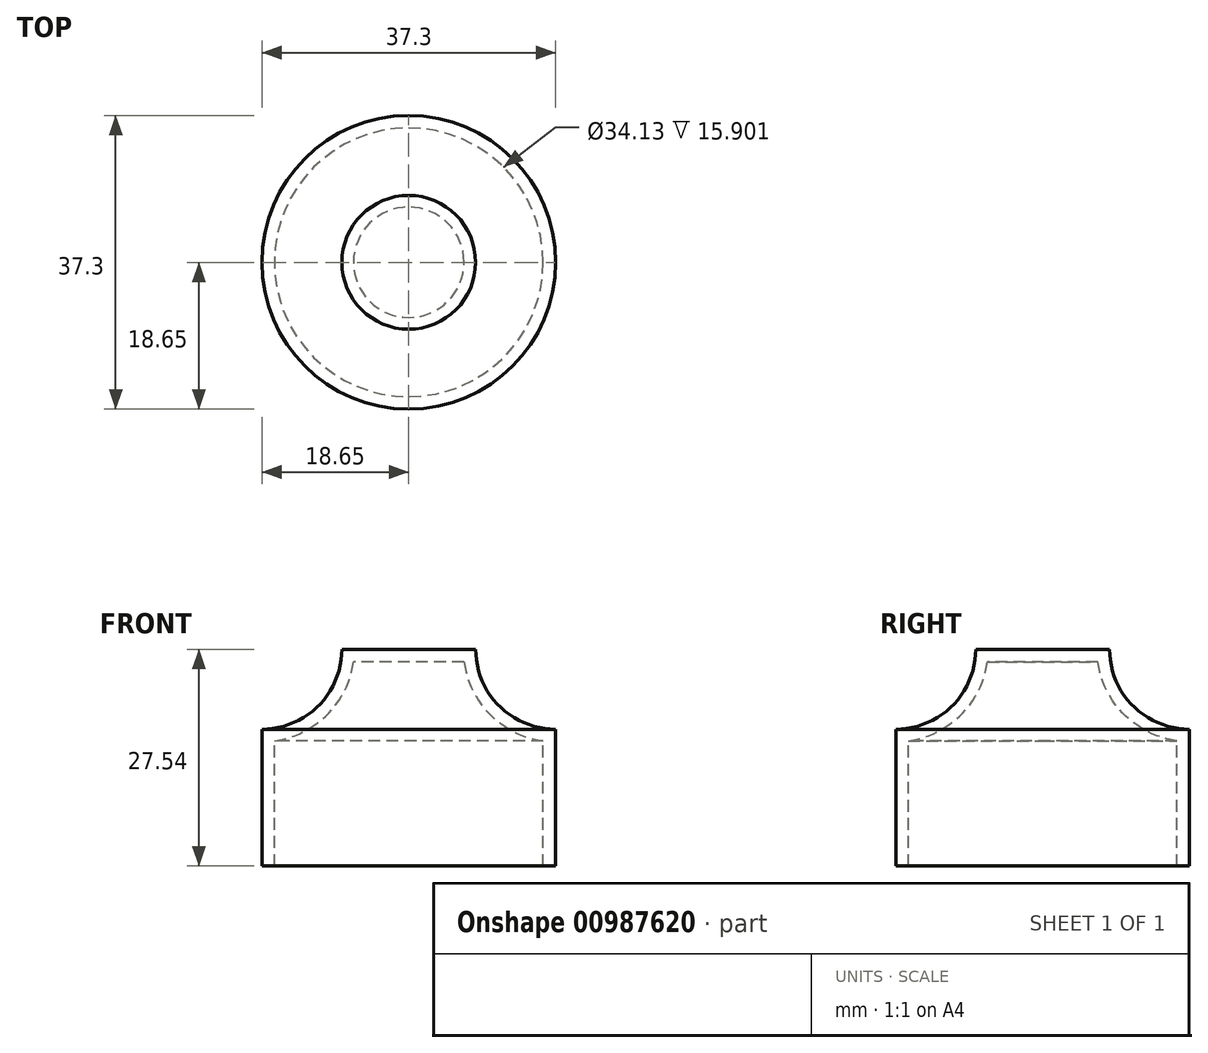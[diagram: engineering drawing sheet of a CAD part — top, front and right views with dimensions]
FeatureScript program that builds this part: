
annotation { "Feature Type Name" : "Feature", "Feature Type Description" : "" }
export const myFeature = defineFeature(function(context is Context, id is Id, definition is map)
    precondition{}
    {
        {
            var Q0;
            Q0=qCreatedBy(makeId("Front.planeOp"),FACE);
            var sketch = newSketch(context, id + "F0", { "sketchPlane" : qUnion([Q0])});
            skLineSegment(sketch, "E0", {"start": v(18.65, 0) * mm, "end": v(18.65, 17.38) * mm});
            skArc(sketch, "E1", {"start": v(8.5, 27.54) * mm, "mid": v(11.47, 20.36) * mm, "end": v(18.65, 17.38) * mm});
            skLineSegment(sketch, "E2", {"start": v(18.65, 17.38) * mm, "end": v(30.29, 17.38) * mm, "construction": true});
            skLineSegment(sketch, "E3", {"start": v(8.5, 27.54) * mm, "end": v(0, 27.54) * mm});
            skLineSegment(sketch, "E4", {"start": v(0, 27.54) * mm, "end": v(0, 25.95) * mm});
            skLineSegment(sketch, "E5", {"start": v(8.5, 27.54) * mm, "end": v(8.5, 39.33) * mm, "construction": true});
            skLineSegment(sketch, "E6.0", {"start": v(7.02, 25.95) * mm, "end": v(0, 25.95) * mm});
            skArc(sketch, "E6.1", {"start": v(7.02, 25.95) * mm, "mid": v(10.35, 19.23) * mm, "end": v(17.07, 15.9) * mm});
            skLineSegment(sketch, "E6.2", {"start": v(17.07, 0) * mm, "end": v(17.07, 15.9) * mm});
            skLineSegment(sketch, "E7", {"start": v(17.07, 0) * mm, "end": v(18.65, 0) * mm});
            skLineSegment(sketch, "E8", {"start": v(10.35, 19.23) * mm, "end": v(11.47, 20.36) * mm, "construction": true});
            skLineSegment(sketch, "E9", {"start": v(0, 0) * mm, "end": v(0, 25.95) * mm, "construction": true});
            skSolve(sketch);
        }
        {
            var Q0;
            Q0 = qSketchRegion(id + "F0", true);
            var Q1;
            Q1=sQuery(id+"F0.wireOp",EDGE,"E4");
            revolve(context, id + "F1", {"surfaceOperationType" : NewSurfaceOperationType.NEW, "entities" : qUnion([Q0]), "axis" : qUnion([Q1]), "revolveType" : RevolveType.FULL});
        }
    });
